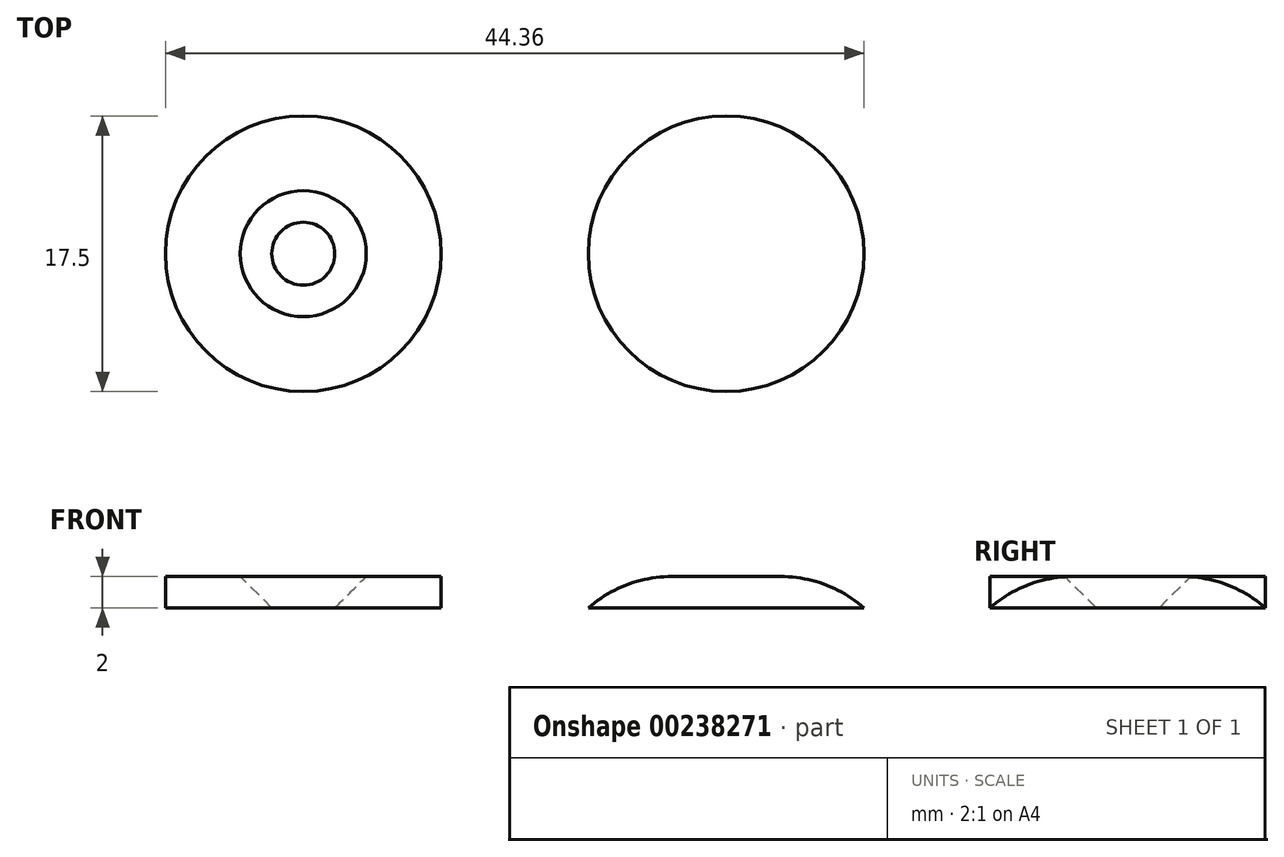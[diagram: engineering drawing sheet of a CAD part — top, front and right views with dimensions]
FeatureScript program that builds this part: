
annotation { "Feature Type Name" : "Feature", "Feature Type Description" : "" }
export const myFeature = defineFeature(function(context is Context, id is Id, definition is map)
    precondition{}
    {
        {
            var Q0;
            Q0=qCreatedBy(makeId("Top.planeOp"),FACE);
            var sketch = newSketch(context, id + "F0", { "sketchPlane" : qUnion([Q0])});
            skCircle(sketch, "E0", {"center": v(0, 0) * mm, "radius": 8.75 * mm});
            skCircle(sketch, "E1", {"center": v(0, 0) * mm, "radius": 2 * mm});
            skCircle(sketch, "E2", {"center": v(0, 0) * mm, "radius": 3.75 * mm, "construction": true});
            skCircle(sketch, "E3", {"center": v(26.86, 0) * mm, "radius": 8.75 * mm});
            skSolve(sketch);
        }
        {
            var Q0;
            Q0=makeQuery(id+"F0.imprint","IMPRINT",FACE,{"disambiguationData":[TD([[makeQuery(id+"F0.imprint","IMPRINT",EDGE,{"derivedFrom":sQuery(id+"F0.wireOp",EDGE,"E0")}),1.0]])]});
            extrude(context, id + "F1", {"entities" : qUnion([Q0]), "depth" : 2 * mm});
        }
        {
            var Q0;
            Q0=makeQuery(id+"F1.opExtrude","CAP_EDGE",EDGE,{"disambiguationData":[OSD([sQuery(id+"F0.wireOp",EDGE,"E1")])],"isStart":false});
            chamfer(context, id + "F2", {"entities" : qUnion([Q0]), "width" : 2 * mm, "tangentPropagation" : true});
        }
        {
            var Q0;
            Q0=makeQuery(id+"F0.imprint","IMPRINT",FACE,{"disambiguationData":[TD([[makeQuery(id+"F0.imprint","IMPRINT",EDGE,{"derivedFrom":sQuery(id+"F0.wireOp",EDGE,"E3")}),1.0]])]});
            extrude(context, id + "F3", {"entities" : qUnion([Q0]), "depth" : 2 * mm});
        }
        {
            var Q0;
            Q0=makeQuery(id+"F3.opExtrude","CAP_EDGE",EDGE,{"disambiguationData":[OSD([sQuery(id+"F0.wireOp",EDGE,"E3")])],"isStart":false});
            fillet(context, id + "F4", {"entities" : qUnion([Q0]), "radius" : 8 * mm, "tangentPropagation" : true, "allowEdgeOverflow" : false});
        }
    });
